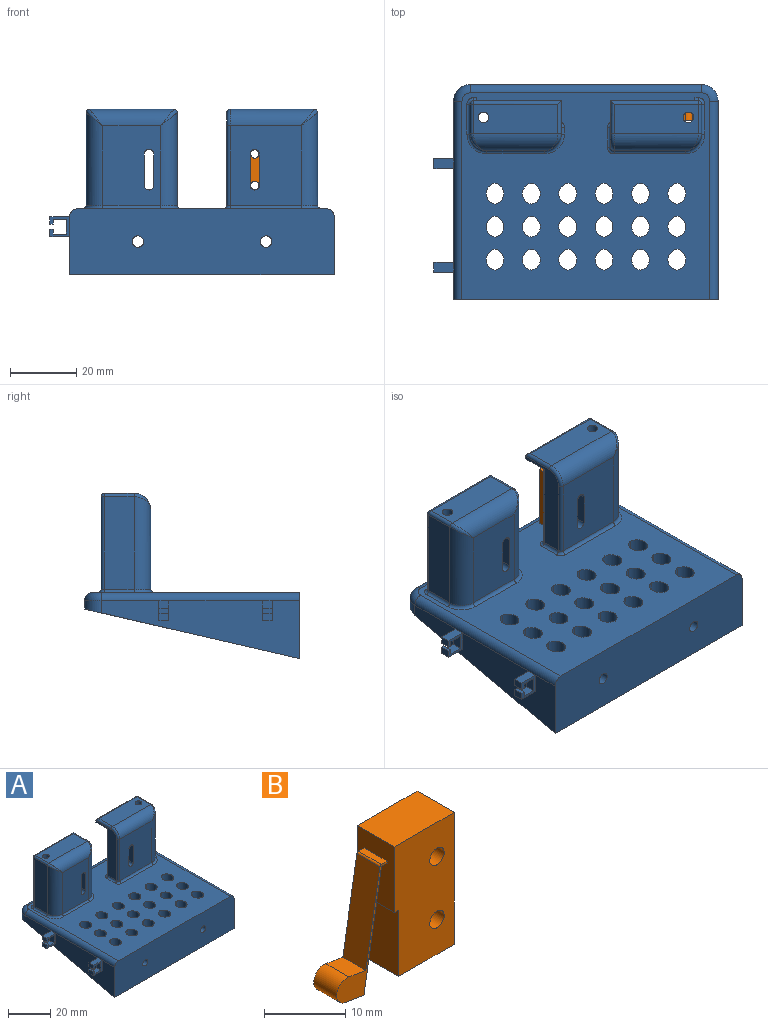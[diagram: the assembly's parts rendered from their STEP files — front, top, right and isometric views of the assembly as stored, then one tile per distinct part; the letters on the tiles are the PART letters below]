
ASSEMBLY  parts=2 mates=1
PART A: 169 faces, bbox 86.6x65.6x50.6 mm
  f0: plane 6x6mm, normal (0,1,0), area 16.6mm2, adj f1,f4,f5,f149,f150,f151,f161,f162
  f1: plane 3x2.25mm, normal (-1,0,0), area 6.8mm2, adj f0,f148,f150,f168
  f2: plane 3x2.25mm, normal (-1,0,0), area 6.7mm2, adj f152,f154,f155,f166
  f3: plane 3x1.48mm, normal (1,0,0), area 4.5mm2, adj f152,f154,f157,f165
  f4: plane 3x1.48mm, normal (1,0,0), area 4.5mm2, adj f0,f148,f164,f167
  f5: plane 60x17.5mm, normal (-1,0,0), area 598.4mm2, adj f0,f38,f43,f46,f55,f148,f150,f152
  f6: plane 73.77x59.97mm, normal (0,0,-1), area 3688.6mm2, adj f17,f18,f19,f20,f21,f22,f23,f24
  f7: cylinder r=1.6mm len=3.2mm, axis (0,0,1), area 10.1mm2, adj f15,f140,f146
  f8: cylinder r=1.6mm len=3.2mm, axis (0,0,1), area 10.1mm2, adj f15,f104,f145
  f9: plane 25.5x9mm, normal (0,0,1), area 221.5mm2, adj f94,f100,f110,f113,f114
  f10: plane 24x17.5mm, normal (0,-1,0), area 387.2mm2, adj f66,f67,f68,f69,f98,f99,f100,f115
  f11: plane 27.2x24.5mm, normal (0,1,0), area 519mm2, adj f13,f59,f66,f67,f68,f69,f93,f103
  f12: plane 28x26.5mm, normal (0,1,0), area 53.5mm2, adj f13,f59,f97,f113,f118,f121
  f13: plane 25.5x8mm, normal (0,0,-1), area 164.2mm2, adj f11,f12,f59,f91,f92,f97,f105,f142
  f14: plane 25.5x9mm, normal (0,0,1), area 221.5mm2, adj f95,f101,f123,f127,f129
  f15: plane 75x62.5mm, normal (0,0,1), area 3602mm2, adj f7,f8,f17,f18,f19,f20,f21,f22
  f16: plane 27.2x24.5mm, normal (0,1,0), area 519mm2, adj f60,f61,f62,f63,f64,f65,f72,f136
  f17: cylinder r=3.2mm len=6.32mm, axis (0,0,-1), area 45.2mm2, adj f6,f15,f90
  f18: cylinder r=3.2mm len=6.32mm, axis (0,0,-1), area 45.2mm2, adj f6,f15,f89
  f19: cylinder r=3.2mm len=6.32mm, axis (0,0,-1), area 45.2mm2, adj f6,f15,f88
  f20: cylinder r=3.2mm len=6.32mm, axis (0,0,-1), area 45.2mm2, adj f6,f15,f87
  f21: cylinder r=3.2mm len=6.32mm, axis (0,0,-1), area 45.2mm2, adj f6,f15,f86
  f22: cylinder r=3.2mm len=6.32mm, axis (0,0,-1), area 45.2mm2, adj f6,f15,f85
  f23: cylinder r=3.2mm len=6.32mm, axis (0,0,-1), area 45.2mm2, adj f6,f15,f84
  f24: cylinder r=3.2mm len=6.32mm, axis (0,0,-1), area 45.2mm2, adj f6,f15,f83
  f25: cylinder r=3.2mm len=6.32mm, axis (0,0,-1), area 45.2mm2, adj f6,f15,f82
  f26: cylinder r=3.2mm len=6.32mm, axis (0,0,-1), area 45.2mm2, adj f6,f15,f81
  f27: cylinder r=3.2mm len=6.32mm, axis (0,0,-1), area 45.2mm2, adj f6,f15,f80
  f28: cylinder r=3.2mm len=6.32mm, axis (0,0,-1), area 45.2mm2, adj f6,f15,f79
  f29: cylinder r=3.2mm len=6.32mm, axis (0,0,-1), area 45.2mm2, adj f6,f15,f78
  f30: cylinder r=3.2mm len=6.32mm, axis (0,0,-1), area 45.2mm2, adj f6,f15,f77
  f31: cylinder r=3.2mm len=6.32mm, axis (0,0,-1), area 45.2mm2, adj f6,f15,f76
  f32: cylinder r=3.2mm len=6.32mm, axis (0,0,-1), area 45.2mm2, adj f6,f15,f75
  f33: cylinder r=3.2mm len=6.32mm, axis (0,0,-1), area 45.2mm2, adj f6,f15,f74
  f34: cylinder r=3.2mm len=6.32mm, axis (0,0,-1), area 45.2mm2, adj f6,f15,f73
  f35: plane 24x21.5mm, normal (0,-1,0), area 483.2mm2, adj f62,f63,f64,f65,f101,f102,f133,f134
  f36: plane 60x17.5mm, normal (1,0,0), area 634.4mm2, adj f38,f43,f47,f51
  f37: plane 71.06x0.03mm, normal (0,0.22,-0.97), area 2mm2, adj f6,f40,f46,f47
  f38: plane 80x20mm, normal (0,-1,0), area 1578.1mm2, adj f5,f15,f36,f43,f44,f45,f51,f55
  f39: plane 70.13x11.86mm, normal (0,1,0), area 810.8mm2, adj f6,f41,f42,f44,f45,f48,f49,f50
  f40: plane 70x2.49mm, normal (0,1,0), area 174.5mm2, adj f37,f46,f47,f53
  f41: plane 48.86x11.28mm, normal (-1,0,0), area 275.6mm2, adj f6,f39,f50
  f42: plane 48.86x11.28mm, normal (1,0,0), area 275.6mm2, adj f6,f39,f48
  f43: plane 80.16x64.49mm, normal (0,0.22,-0.97), area 559.4mm2, adj f5,f36,f38,f46,f47,f48,f49,f50
  f44: cylinder r=1.75mm len=5mm, axis (0,-1,0), area 55mm2, adj f38,f39
  f45: cylinder r=1.75mm len=5mm, axis (0,-1,0), area 55mm2, adj f38,f39
  f46: cylinder r=5mm len=5mm, axis (0,0,-1), area 23.1mm2, adj f5,f6,f37,f40,f43,f48,f54
  f47: cylinder r=5mm len=5mm, axis (0,0,1), area 23.1mm2, adj f6,f36,f37,f40,f43,f50,f52
  f48: cylinder r=2.5mm len=62.15mm, axis (0,0.97,0.22), area 227.6mm2, adj f6,f39,f42,f43,f46,f49
  f49: cylinder r=2.5mm len=75mm, axis (-1,0,0), area 242.3mm2, adj f39,f43,f48,f50
  f50: cylinder r=2.5mm len=62.15mm, axis (0,-0.97,-0.22), area 227.6mm2, adj f6,f39,f41,f43,f47,f49
  f51: cylinder r=2.5mm len=60mm, axis (0,-1,0), area 235.6mm2, adj f15,f36,f38,f52
  f52: torus R=2.5mm, axis (0,0,1), area 25.2mm2, adj f15,f47,f51,f53
  f53: cylinder r=2.5mm len=70mm, axis (1,0,0), area 274.9mm2, adj f15,f40,f52,f54
  f54: torus R=2.5mm, axis (0,0,1), area 25.2mm2, adj f15,f46,f53,f55
  f55: cylinder r=2.5mm len=60mm, axis (0,1,0), area 235.6mm2, adj f5,f15,f38,f54,f149,f153
  f56: plane 28x9mm, normal (1,0,0), area 252mm2, adj f102,f123,f125,f130
  f57: plane 28x26.5mm, normal (0,1,0), area 53.5mm2, adj f60,f61,f96,f125,f126,f127
  f58: plane 28x9mm, normal (-1,0,0), area 252mm2, adj f99,f114,f118,f119
  f59: plane 28x8mm, normal (1,0,0), area 152mm2, adj f11,f12,f13,f15,f92,f93,f103,f121
  f60: plane 25.5x8mm, normal (0,0,-1), area 164.2mm2, adj f16,f57,f61,f70,f71,f96,f136,f143
  f61: plane 28x8mm, normal (-1,0,0), area 152mm2, adj f15,f16,f57,f60,f71,f72,f126,f141
  f62: plane 9.5x8mm, normal (1,0,0), area 76mm2, adj f16,f35,f63,f64
  f63: cylinder r=1.4mm len=8mm, axis (0,1,0), area 35.2mm2, adj f16,f35,f62,f65
  f64: cylinder r=1.4mm len=8mm, axis (0,1,0), area 35.2mm2, adj f16,f35,f62,f65
  f65: plane 9.5x8mm, normal (-1,0,0), area 76mm2, adj f16,f35,f63,f64
  f66: plane 9.5x8mm, normal (1,0,0), area 76mm2, adj f10,f11,f67,f68
  f67: cylinder r=1.4mm len=8mm, axis (0,1,0), area 35.2mm2, adj f10,f11,f66,f69
  f68: cylinder r=1.4mm len=8mm, axis (0,1,0), area 35.2mm2, adj f10,f11,f66,f69
  f69: plane 9.5x8mm, normal (-1,0,0), area 76mm2, adj f10,f11,f67,f68
  f70: plane 22x1mm, normal (-1,0,0), area 22mm2, adj f60,f71,f72,f143
  f71: cylinder r=2mm len=22mm, axis (0,0,1), area 138.2mm2, adj f60,f61,f70,f72
  f72: plane 5x4mm, normal (0,0,-1), area 6.5mm2, adj f16,f61,f70,f71,f95,f143
  f73: cylinder r=3.2mm len=6.32mm, axis (0,0,-1), area 45.2mm2, adj f6,f15,f34
  f74: cylinder r=3.2mm len=6.32mm, axis (0,0,-1), area 45.2mm2, adj f6,f15,f33
  f75: cylinder r=3.2mm len=6.32mm, axis (0,0,-1), area 45.2mm2, adj f6,f15,f32
  f76: cylinder r=3.2mm len=6.32mm, axis (0,0,-1), area 45.2mm2, adj f6,f15,f31
  f77: cylinder r=3.2mm len=6.32mm, axis (0,0,-1), area 45.2mm2, adj f6,f15,f30
  f78: cylinder r=3.2mm len=6.32mm, axis (0,0,-1), area 45.2mm2, adj f6,f15,f29
  f79: cylinder r=3.2mm len=6.32mm, axis (0,0,-1), area 45.2mm2, adj f6,f15,f28
  f80: cylinder r=3.2mm len=6.32mm, axis (0,0,-1), area 45.2mm2, adj f6,f15,f27
  f81: cylinder r=3.2mm len=6.32mm, axis (0,0,-1), area 45.2mm2, adj f6,f15,f26
  f82: cylinder r=3.2mm len=6.32mm, axis (0,0,-1), area 45.2mm2, adj f6,f15,f25
  f83: cylinder r=3.2mm len=6.32mm, axis (0,0,-1), area 45.2mm2, adj f6,f15,f24
  f84: cylinder r=3.2mm len=6.32mm, axis (0,0,-1), area 45.2mm2, adj f6,f15,f23
  f85: cylinder r=3.2mm len=6.32mm, axis (0,0,-1), area 45.2mm2, adj f6,f15,f22
  f86: cylinder r=3.2mm len=6.32mm, axis (0,0,-1), area 45.2mm2, adj f6,f15,f21
  f87: cylinder r=3.2mm len=6.32mm, axis (0,0,-1), area 45.2mm2, adj f6,f15,f20
  f88: cylinder r=3.2mm len=6.32mm, axis (0,0,-1), area 45.2mm2, adj f6,f15,f19
  f89: cylinder r=3.2mm len=6.32mm, axis (0,0,-1), area 45.2mm2, adj f6,f15,f18
  f90: cylinder r=3.2mm len=6.32mm, axis (0,0,-1), area 45.2mm2, adj f6,f15,f17
  f91: plane 22x1mm, normal (1,0,0), area 22mm2, adj f13,f92,f93,f142
  f92: cylinder r=2mm len=22mm, axis (0,0,1), area 138.2mm2, adj f13,f59,f91,f93
  f93: plane 5x4mm, normal (0,0,-1), area 6.5mm2, adj f11,f59,f91,f92,f94,f142
  f94: cylinder r=1.6mm len=24mm, axis (0,0,1), area 241.3mm2, adj f9,f93
  f95: cylinder r=1.6mm len=24mm, axis (0,0,1), area 241.3mm2, adj f14,f72
  f96: plane 28x14mm, normal (-1,0,0), area 172.6mm2, adj f57,f60,f129,f131,f133,f136,f137
  f97: plane 28x10mm, normal (1,0,0), area 64mm2, adj f12,f13,f98,f105,f109,f110
  f98: cylinder r=5mm len=28mm, axis (0,0,1), area 208.5mm2, adj f10,f97,f108,f112
  f99: cylinder r=5mm len=28mm, axis (0,0,1), area 208.5mm2, adj f10,f58,f111,f117
  f100: cylinder r=5mm len=25.5mm, axis (-1,0,0), area 177.4mm2, adj f9,f10,f108,f111
  f101: cylinder r=5mm len=25.5mm, axis (-1,0,0), area 188.9mm2, adj f14,f35,f122,f131
  f102: cylinder r=5mm len=28mm, axis (0,0,-1), area 208.5mm2, adj f35,f56,f122,f132
  f103: cylinder r=1mm len=1mm, axis (1,0,0), area 1.2mm2, adj f11,f15,f59,f104
  f104: bspline ~2.5x1mm, area 2.9mm2, adj f8,f11,f103,f106
  f105: cylinder r=1mm len=27mm, axis (0,0,-1), area 42.4mm2, adj f11,f13,f97,f107
  f106: cylinder r=1mm len=21.25mm, axis (1,0,0), area 33.4mm2, adj f11,f15,f104,f107
  f107: torus R=2mm, axis (0,0,1), area 3.4mm2, adj f15,f105,f106,f109
  f108: bspline ~5.2x5mm, area 8.5mm2, adj f98,f100,f110
  f109: cylinder r=1mm len=2mm, axis (0,-1,0), area 3.1mm2, adj f15,f97,f107,f112
  f110: cylinder r=1mm len=10mm, axis (0,1,0), area 15.1mm2, adj f9,f97,f108,f113
  f111: bspline ~5.78x5mm, area 8.5mm2, adj f99,f100,f114
  f112: torus R=6mm, axis (0,0,1), area 13.2mm2, adj f15,f98,f109,f115
  f113: cylinder r=1mm len=26.5mm, axis (1,0,0), area 41.1mm2, adj f9,f12,f110,f116
  f114: cylinder r=1mm len=9mm, axis (0,1,0), area 14.1mm2, adj f9,f58,f111,f116
  f115: cylinder r=1mm len=17.5mm, axis (1,0,0), area 27.5mm2, adj f10,f15,f112,f117
  f116: sphere r=1mm, area 1.6mm2, adj f113,f114,f118
  f117: torus R=6mm, axis (0,0,1), area 13.2mm2, adj f15,f99,f115,f119
  f118: cylinder r=1mm len=28mm, axis (0,0,-1), area 44mm2, adj f12,f58,f116,f120
  f119: cylinder r=1mm len=9mm, axis (0,-1,0), area 14.1mm2, adj f15,f58,f117,f120
  f120: torus R=2mm, axis (0,0,1), area 3.4mm2, adj f15,f118,f119,f121
  f121: cylinder r=1mm len=1mm, axis (-1,0,0), area 1.6mm2, adj f12,f15,f59,f120
  f122: bspline ~5.78x5mm, area 8.5mm2, adj f101,f102,f123
  f123: cylinder r=1mm len=9mm, axis (0,-1,0), area 14.1mm2, adj f14,f56,f122,f124
  f124: sphere r=1mm, area 1.6mm2, adj f123,f125,f127
  f125: cylinder r=1mm len=28mm, axis (0,0,1), area 44mm2, adj f56,f57,f124,f128
  f126: cylinder r=1mm len=1mm, axis (-1,0,0), area 1.6mm2, adj f15,f57,f61,f128
  f127: cylinder r=1mm len=26.5mm, axis (1,0,0), area 41.1mm2, adj f14,f57,f124,f129
  f128: torus R=2mm, axis (0,0,1), area 3.4mm2, adj f15,f125,f126,f130
  f129: cylinder r=1mm len=10mm, axis (0,-1,0), area 15.1mm2, adj f14,f96,f127,f131
  f130: cylinder r=1mm len=9mm, axis (0,1,0), area 14.1mm2, adj f15,f56,f128,f132
  f131: torus R=4mm, axis (1,0,0), area 11.4mm2, adj f96,f101,f129,f133
  f132: torus R=6mm, axis (0,0,1), area 13.2mm2, adj f15,f102,f130,f134
  f133: cylinder r=1mm len=24mm, axis (0,0,-1), area 37.7mm2, adj f35,f96,f131,f135
  f134: cylinder r=1mm len=21.5mm, axis (1,0,0), area 33.8mm2, adj f15,f35,f132,f135
  f135: torus R=2mm, axis (0,0,1), area 3.4mm2, adj f15,f133,f134,f137
  f136: cylinder r=1mm len=27mm, axis (0,0,1), area 42.4mm2, adj f16,f60,f96,f138
  f137: cylinder r=1mm len=6mm, axis (0,1,0), area 9.4mm2, adj f15,f96,f135,f138
  f138: torus R=2mm, axis (0,0,1), area 3.4mm2, adj f15,f136,f137,f139
  f139: cylinder r=1mm len=21.25mm, axis (1,0,0), area 33.4mm2, adj f15,f16,f138,f140
  f140: bspline ~2.5x1mm, area 2.9mm2, adj f7,f16,f139,f141
  f141: cylinder r=1mm len=1mm, axis (1,0,0), area 1.2mm2, adj f15,f16,f61,f140
  f142: cylinder r=1mm len=22mm, axis (0,0,-1), area 34.6mm2, adj f11,f13,f91,f93
  f143: cylinder r=1mm len=22mm, axis (0,0,-1), area 34.6mm2, adj f16,f60,f70,f72
  f144: cylinder r=3mm len=6mm, axis (0,0,-1), area 75.4mm2, adj f6,f145
  f145: plane 6x6mm, normal (0,0,-1), area 20.2mm2, adj f8,f144
  f146: plane 6x6mm, normal (0,0,-1), area 20.2mm2, adj f7,f147
  f147: cylinder r=3mm len=6mm, axis (0,0,-1), area 75.4mm2, adj f6,f146
  f148: plane 6x6mm, normal (0,-1,0), area 16.6mm2, adj f1,f4,f5,f149,f150,f151,f161,f162
  f149: plane 6x3mm, normal (0,0,1), area 18mm2, adj f0,f55,f148,f151
  f150: plane 6x3mm, normal (0,0,-1), area 18mm2, adj f0,f1,f5,f148
  f151: plane 3x2.25mm, normal (-1,0,0), area 6.8mm2, adj f0,f148,f149,f167
  f152: plane 6x6mm, normal (0,-1,0), area 16.6mm2, adj f2,f3,f5,f153,f155,f156,f157,f158
  f153: plane 6x3mm, normal (0,0,1), area 18mm2, adj f55,f152,f154,f156
  f154: plane 6x6mm, normal (0,1,0), area 16.6mm2, adj f2,f3,f5,f153,f155,f156,f157,f158
  f155: plane 6x3mm, normal (0,0,-1), area 18mm2, adj f2,f5,f152,f154
  f156: plane 3x2.25mm, normal (-1,0,0), area 6.7mm2, adj f152,f153,f154,f165
  f157: plane 4x3mm, normal (0,0,-1), area 12mm2, adj f3,f152,f154,f160
  f158: plane 3x1.48mm, normal (1,0,0), area 4.5mm2, adj f152,f154,f159,f166
  f159: plane 4x3mm, normal (0,0,1), area 12mm2, adj f152,f154,f158,f160
  f160: plane 4.47x3mm, normal (-1,0,0), area 13.4mm2, adj f152,f154,f157,f159
  f161: plane 4.47x3mm, normal (-1,0,0), area 13.4mm2, adj f0,f148,f162,f164
  f162: plane 4x3mm, normal (0,0,1), area 12mm2, adj f0,f148,f161,f163
  f163: plane 3x1.48mm, normal (1,0,0), area 4.5mm2, adj f0,f148,f162,f168
  f164: plane 4x3mm, normal (0,0,-1), area 12mm2, adj f0,f4,f148,f161
  f165: plane 3x1mm, normal (0,0,-1), area 3mm2, adj f3,f152,f154,f156
  f166: plane 3x1mm, normal (0,0,1), area 3mm2, adj f2,f152,f154,f158
  f167: plane 3x1mm, normal (0,0,-1), area 3mm2, adj f0,f4,f148,f151
  f168: plane 3x1mm, normal (0,0,1), area 3mm2, adj f0,f1,f148,f163
PART B: 20 faces, bbox 19.2x6.5x21 mm
  f0: plane 18.21x8.79mm, normal (0,-1,0), area 21.3mm2, adj f1,f3,f11,f12,f13,f14,f15,f16
  f1: plane 4x3.23mm, normal (-0.17,0,-0.99), area 13.1mm2, adj f0,f10,f15,f19
  f2: plane 10.45x6.45mm, normal (0,0,1), area 67.4mm2, adj f3,f5,f6,f7
  f3: plane 9.9x6.45mm, normal (-1,0,0), area 62.7mm2, adj f0,f2,f6,f7,f8,f10,f11,f12
  f4: plane 9.7x6.45mm, normal (0,0,-1), area 62.6mm2, adj f5,f6,f7,f9
  f5: plane 19.9x6.45mm, normal (1,0,0), area 128.4mm2, adj f2,f4,f6,f7
  f6: plane 19.9x10.45mm, normal (0,-1,0), area 190.6mm2, adj f2,f3,f4,f5,f8,f9,f17,f18
  f7: plane 19.9x10.45mm, normal (0,1,0), area 190.6mm2, adj f2,f3,f4,f5,f8,f9,f17,f18
  f8: plane 6.45x0.75mm, normal (0,0,-1), area 4.8mm2, adj f3,f6,f7,f9
  f9: plane 10x6.45mm, normal (-1,0,0), area 64.5mm2, adj f4,f6,f7,f8
  f10: plane 18.21x8.79mm, normal (0,1,0), area 21.3mm2, adj f1,f3,f11,f12,f13,f14,f15,f16
  f11: plane 4x1mm, normal (0,0,-1), area 4mm2, adj f0,f3,f10,f15
  f12: plane 4x1mm, normal (0,0,1), area 4mm2, adj f0,f3,f10,f13
  f13: cylinder r=0.28mm len=4mm, axis (0,-1,0), area 1.6mm2, adj f0,f10,f12,f14
  f14: plane 14.39x4mm, normal (-0.99,0,0.17), area 58.4mm2, adj f0,f10,f13,f16
  f15: plane 17.93x4mm, normal (0.99,0,-0.17), area 72.8mm2, adj f0,f1,f10,f11
  f16: plane 4x2.96mm, normal (0.17,0,0.99), area 12mm2, adj f0,f10,f14,f19
  f17: cylinder r=1.25mm len=6.45mm, axis (0,-1,0), area 50.7mm2, adj f6,f7
  f18: cylinder r=1.25mm len=6.45mm, axis (0,-1,0), area 50.7mm2, adj f6,f7
  f19: cylinder r=1.8mm len=4mm, axis (0,-1,0), area 22.6mm2, adj f0,f1,f10,f16
PLACE A t=(-10.2,-0.52,6.69)mm
PLACE B rot(axis=(0,0,1),180deg) t=(8.03,19.98,23.39)mm
MATE fastened B.f18 <-> A.f64  axis (0,-1,0) through (5.8,19.98,28.19)mm
